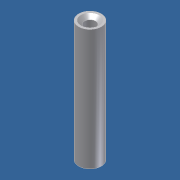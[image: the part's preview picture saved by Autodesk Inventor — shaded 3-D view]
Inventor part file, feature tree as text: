
AUTODESK INVENTOR PART (.ipt)
format: ipt  version: unknown  size: 169,472 bytes
history: native  units: mm
features: revolve x1, chamfer x1, sketch x1
ambient origin geometry x8: Origin, YZ Plane, XZ Plane, XY Plane, X Axis, Y Axis, Z Axis, Center Point
feature tree (3):
  revolve  "Revolution1"  [1 undecoded]
  chamfer  "Chamfer1"  Angle=90.0deg  [1 undecoded]
  sketch  "Sketch2"  dims[d0=3.175mm d1=1.5875mm d2=90.0deg d3=90.0deg d4=20.0mm d5=90.0deg d6=1.0mm d7=2.0mm d8=45.0deg]
note: 2 required parameter values undecoded (feature->parameter linkage not recoverable at this tier; creation-order binding heuristic only, values carry confidence <= 0.55)